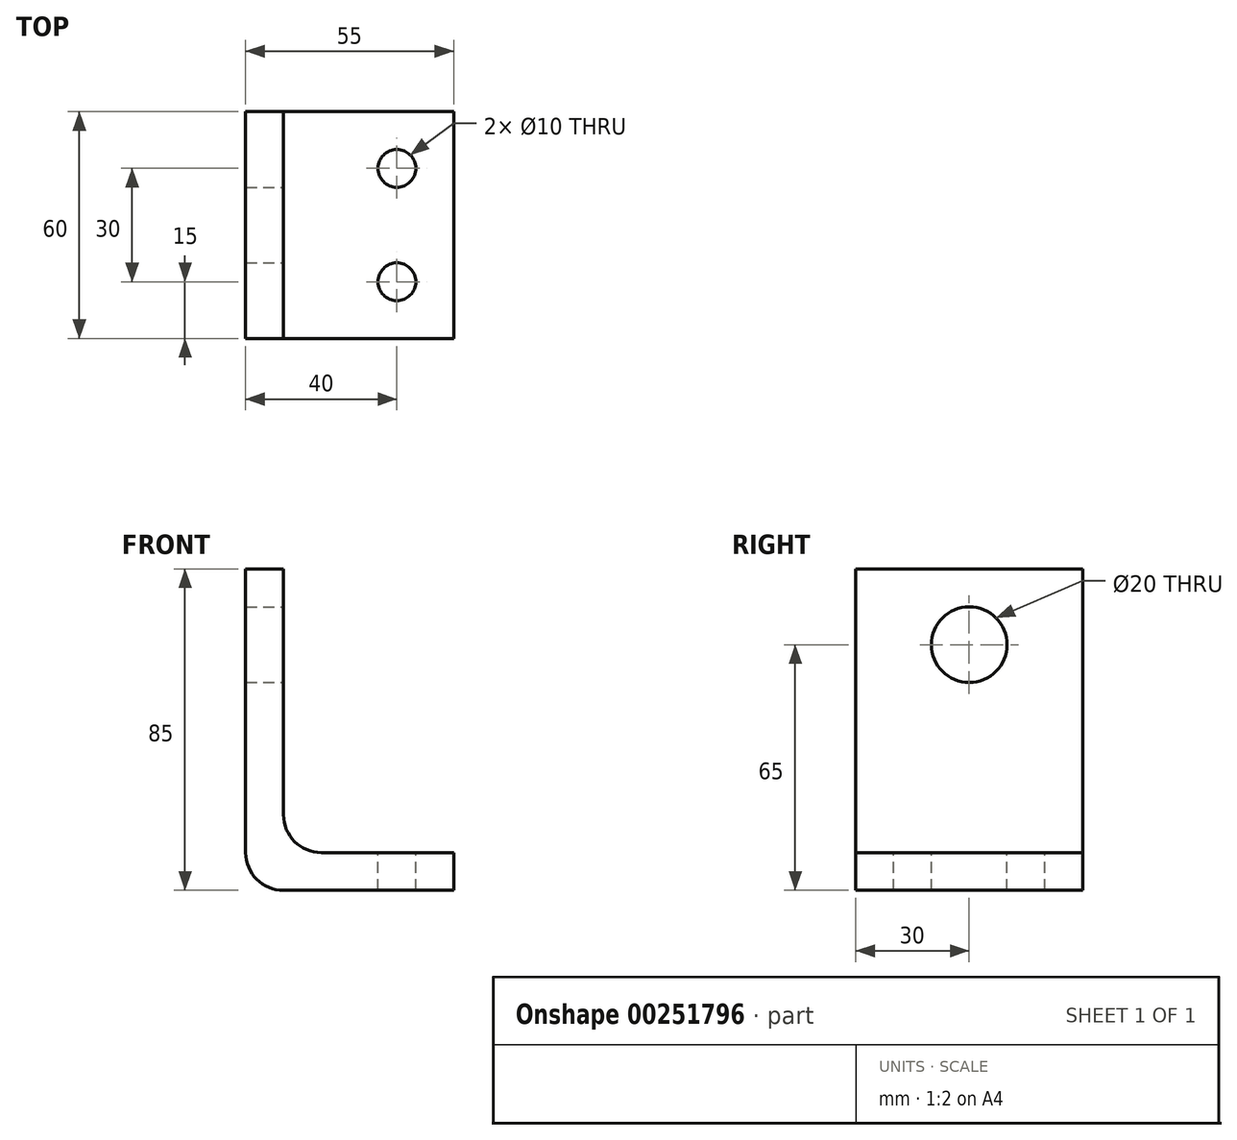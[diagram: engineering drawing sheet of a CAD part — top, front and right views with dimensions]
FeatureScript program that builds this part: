
annotation { "Feature Type Name" : "Feature", "Feature Type Description" : "" }
export const myFeature = defineFeature(function(context is Context, id is Id, definition is map)
    precondition{}
    {
        {
            var Q0;
            Q0=qCreatedBy(makeId("Right.planeOp"),FACE);
            var sketch = newSketch(context, id + "F0", { "sketchPlane" : qUnion([Q0])});
            skLineSegment(sketch, "E0.bottom", {"start": v(-30, 5) * mm, "end": v(30, 5) * mm});
            skLineSegment(sketch, "E0.top", {"start": v(-30, -5) * mm, "end": v(30, -5) * mm});
            skLineSegment(sketch, "E0.left", {"start": v(-30, 5) * mm, "end": v(-30, -5) * mm});
            skLineSegment(sketch, "E0.right", {"start": v(30, 5) * mm, "end": v(30, -5) * mm});
            skPoint(sketch, "E0.middle", {"position": v(0, 0) * mm});
            skSolve(sketch);
        }
        {
            var Q0;
            Q0=qCreatedBy(makeId("Front.planeOp"),FACE);
            var sketch = newSketch(context, id + "F1", { "sketchPlane" : qUnion([Q0])});
            skLineSegment(sketch, "E1", {"start": v(0, 0) * mm, "end": v(-50, 0) * mm});
            skLineSegment(sketch, "E2", {"start": v(-50, 0) * mm, "end": v(-50, 80) * mm});
            skSolve(sketch);
        }
        {
            var Q0;
            Q0=makeQuery(id+"F0.imprint","IMPRINT",FACE,{"disambiguationData":[TD([[makeQuery(id+"F0.imprint","IMPRINT",EDGE,{"derivedFrom":sQuery(id+"F0.wireOp",EDGE,"E0.bottom")}),-1.0]])]});
            var Q1;
            Q1=sQuery(id+"F1.wireOp",EDGE,"E1");
            var Q2;
            Q2=sQuery(id+"F1.wireOp",EDGE,"E2");
            sweep(context, id + "F2", {"profiles" : qUnion([Q0]), "path" : qUnion([Q1, Q2])});
        }
        {
            var Q0;
            Q0=makeQuery(id+"F2.opSweep","MID_CAP_EDGE",EDGE,{"disambiguationData":[OSD([sQuery(id+"F0.wireOp",EDGE,"E0.bottom"),sQuery(id+"F1.wireOp",VERTEX,"E2.start")])],"capPos":1.0});
            var Q1;
            Q1=makeQuery(id+"F2.opSweep","MID_CAP_EDGE",EDGE,{"disambiguationData":[OSD([sQuery(id+"F0.wireOp",EDGE,"E0.top"),sQuery(id+"F1.wireOp",VERTEX,"E2.start")])],"capPos":1.0});
            fillet(context, id + "F3", {"entities" : qUnion([Q0, Q1]), "radius" : 10 * mm, "tangentPropagation" : true, "allowEdgeOverflow" : false});
        }
        {
            var Q0;
            Q0=makeQuery(id+"F2.opSweep","SWEPT_FACE",FACE,{"disambiguationData":[OSD([sQuery(id+"F0.wireOp",EDGE,"E0.bottom"),sQuery(id+"F1.wireOp",EDGE,"E2")])]});
            var sketch = newSketch(context, id + "F4", { "sketchPlane" : qUnion([Q0])});
            skCircle(sketch, "E3", {"center": v(0, 60) * mm, "radius": 10 * mm});
            skSolve(sketch);
        }
        {
            var Q0;
            Q0 = qSketchRegion(id + "F4", true);
            extrude(context, id + "F5", {"entities" : qUnion([Q0]), "operationType" : NewBodyOperationType.REMOVE, "endBound" : BoundingType.THROUGH_ALL, "oppositeDirection" : true, "depth" : 25 * mm});
        }
        {
            var Q0;
            Q0=makeQuery(id+"F2.opSweep","SWEPT_FACE",FACE,{"disambiguationData":[OSD([sQuery(id+"F0.wireOp",EDGE,"E0.bottom"),sQuery(id+"F1.wireOp",EDGE,"E1")])]});
            var sketch = newSketch(context, id + "F6", { "sketchPlane" : qUnion([Q0])});
            skCircle(sketch, "E4", {"center": v(-15, 15) * mm, "radius": 5 * mm});
            skSolve(sketch);
        }
        {
            var Q0;
            Q0 = qSketchRegion(id + "F6", true);
            extrude(context, id + "F7", {"entities" : qUnion([Q0]), "operationType" : NewBodyOperationType.REMOVE, "oppositeDirection" : true, "depth" : 25 * mm});
        }
        {
            var Q0;
            Q0=makeQuery(id+"F2.opSweep","SWEPT_FACE",FACE,{"disambiguationData":[OSD([sQuery(id+"F0.wireOp",EDGE,"E0.bottom"),sQuery(id+"F1.wireOp",EDGE,"E1")])]});
            var sketch = newSketch(context, id + "F8", { "sketchPlane" : qUnion([Q0])});
            skCircle(sketch, "E5", {"center": v(-15, -15) * mm, "radius": 5 * mm});
            skSolve(sketch);
        }
        {
            var Q0;
            Q0 = qSketchRegion(id + "F8", true);
            extrude(context, id + "F9", {"entities" : qUnion([Q0]), "operationType" : NewBodyOperationType.REMOVE, "oppositeDirection" : true, "depth" : 25 * mm});
        }
    });
